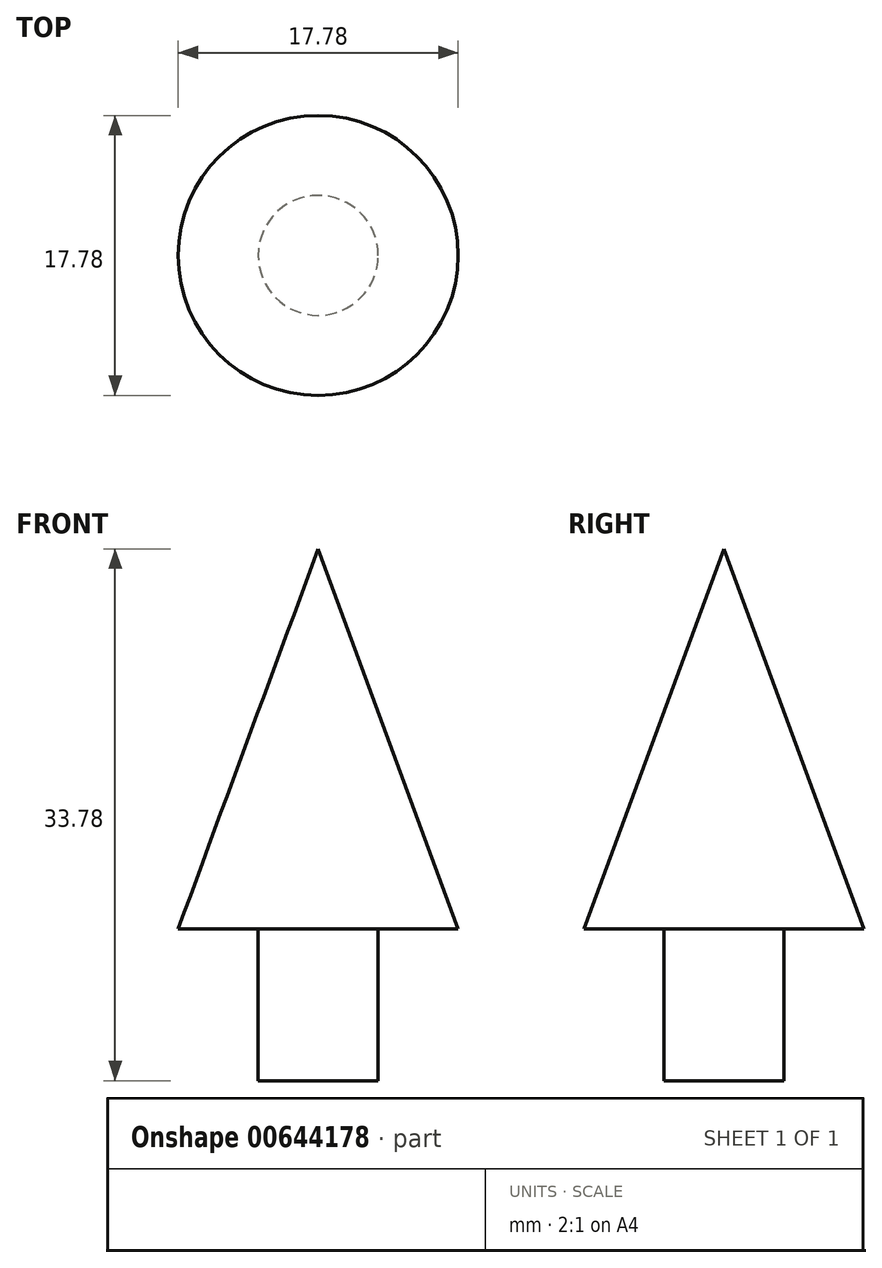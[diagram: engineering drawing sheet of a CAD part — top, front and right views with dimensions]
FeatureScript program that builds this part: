
annotation { "Feature Type Name" : "Feature", "Feature Type Description" : "" }
export const myFeature = defineFeature(function(context is Context, id is Id, definition is map)
    precondition{}
    {
        {
            var Q0;
            Q0=qCreatedBy(makeId("Front.planeOp"),FACE);
            var sketch = newSketch(context, id + "F0", { "sketchPlane" : qUnion([Q0])});
            skLineSegment(sketch, "E0", {"start": v(8.9, 0) * mm, "end": v(0, 24.13) * mm});
            skLineSegment(sketch, "E1", {"start": v(0, 24.13) * mm, "end": v(0, 0) * mm});
            skLineSegment(sketch, "E2", {"start": v(8.9, 0) * mm, "end": v(3.8, 0) * mm});
            skLineSegment(sketch, "E3", {"start": v(3.8, 0) * mm, "end": v(3.8, -9.65) * mm});
            skLineSegment(sketch, "E4", {"start": v(0, 0) * mm, "end": v(0, -9.65) * mm});
            skLineSegment(sketch, "E5", {"start": v(0, -9.65) * mm, "end": v(3.8, -9.65) * mm});
            skSolve(sketch);
        }
        {
            var Q0;
            Q0=makeQuery(id+"F0.imprint","IMPRINT",FACE,{"disambiguationData":[TD([[makeQuery(id+"F0.imprint","IMPRINT",EDGE,{"derivedFrom":sQuery(id+"F0.wireOp",EDGE,"E0")}),1.0]])]});
            var Q1;
            Q1=sQuery(id+"F0.wireOp",EDGE,"E1");
            revolve(context, id + "F1", {"entities" : qUnion([Q0]), "axis" : qUnion([Q1]), "revolveType" : RevolveType.FULL});
        }
    });
